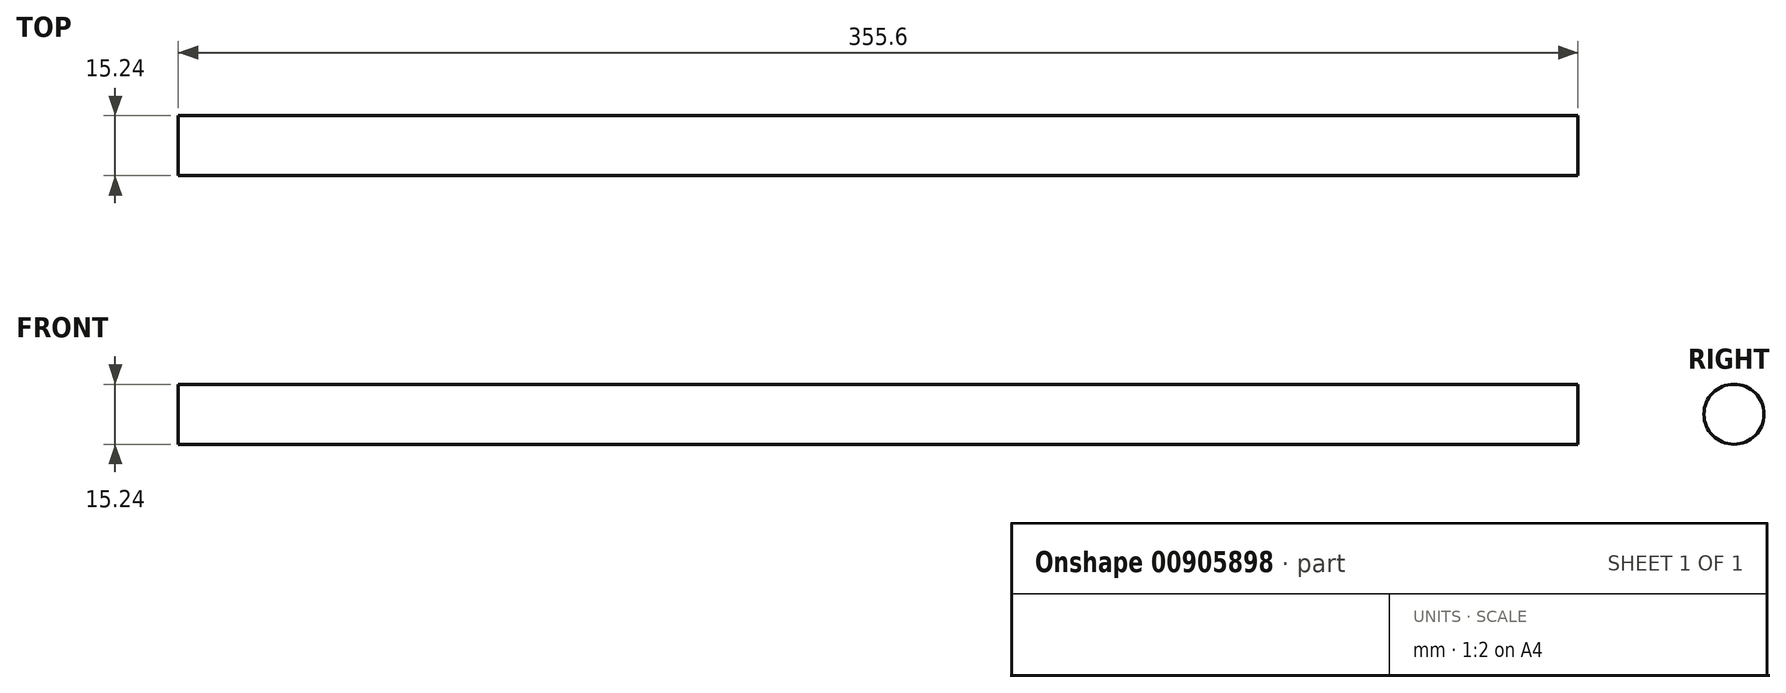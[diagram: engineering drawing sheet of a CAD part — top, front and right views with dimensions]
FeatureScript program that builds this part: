
annotation { "Feature Type Name" : "Feature", "Feature Type Description" : "" }
export const myFeature = defineFeature(function(context is Context, id is Id, definition is map)
    precondition{}
    {
        {
            var Q0;
            Q0=qCreatedBy(makeId("Right.planeOp"),FACE);
            var sketch = newSketch(context, id + "F0", { "sketchPlane" : qUnion([Q0])});
            skCircle(sketch, "E0", {"center": v(0, 0) * mm, "radius": 7.62 * mm});
            skSolve(sketch);
        }
        {
            var Q0;
            Q0 = qSketchRegion(id + "F0", true);
            extrude(context, id + "F1", {"entities" : qUnion([Q0]), "depth" : 355.6 * mm, "offsetDistance" : 25.4 * mm});
        }
    });
